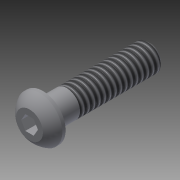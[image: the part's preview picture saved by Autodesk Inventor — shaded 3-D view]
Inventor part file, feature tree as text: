
AUTODESK INVENTOR PART (.ipt)
format: ipt  version: 2015 (Build 190159000, 159)  size: 119,296 bytes
history: native  units: in
note: dims shown in document units (in); Inventor stores cm internally (conversion verified against a paired STEP export)
features: sketch x2, revolve x1, chamfer x1, extrude x1, thread x1
ambient origin geometry x8: Origin, YZ Plane, XZ Plane, XY Plane, X Axis, Y Axis, Z Axis, Center Point
bodies: Solid1 (feature_tree)
feature tree (6):
  revolve  "Revolution1"  [1 undecoded]
  chamfer  "Chamfer1"  Distance=0.125in
  extrude  "Extrusion1"  TaperAngle=90.0deg  [1 undecoded]
  thread  "Thread1"  [1 undecoded]
  sketch  "Sketch1"  dims[d0=0.125in d1=0.211in]
  sketch  "Sketch2"  dims[d2=0.031in d3=0.125in d7=90.0deg d8=0.125in d9=0.236in d10=0.03in d11=0.125in d12=45.0deg d14=0.1562in d15=0.111in d16=0.0in d17=0.75in d18=0.0in d20=1.0in]
note: 3 required parameter values undecoded (feature->parameter linkage not recoverable at this tier; creation-order binding heuristic only, values carry confidence <= 0.55)